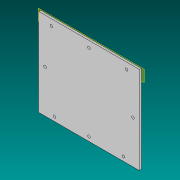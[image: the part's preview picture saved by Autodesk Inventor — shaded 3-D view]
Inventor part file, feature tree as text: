
AUTODESK INVENTOR PART (.ipt)
format: ipt  version: 2019 (Build 230136000, 136)  size: 124,416 bytes
history: native  units: mm
features: reference x16, extrude x5, sketch x5, other x5, plane x1
ambient origin geometry x8: Origin, YZ Plane, XZ Plane, XY Plane, X Axis, Y Axis, Z Axis, Center Point
bodies: Solid1 (feature_tree)
feature tree (32):
  plane  "Work Plane1"
  extrude  "Extrusion1"  Depth=2.0mm
  extrude  "Extrusion2"  Depth=2.5mm
  extrude  "Extrusion3"  Depth=2.5mm
  extrude  "Extrusion4"  Depth=2.0mm TaperAngle=0.0deg
  extrude  "Extrusion5"  Depth=2.0mm TaperAngle=0.0deg
  sketch  "Sketch1"  dims[d0=2.0mm d1=0.0mm d2=2.5mm]
  reference  "Reference1"
  reference  "Reference2"
  reference  "Reference3"
  reference  "Reference4"
  reference  "Reference5"
  reference  "Reference6"
  reference  "Reference7"
  reference  "Reference8"
  reference  "Reference9"
  reference  "Reference10"
  reference  "Reference11"
  reference  "Reference12"
  reference  "Reference13"
  sketch  "Sketch2"  dims[d3=2.5mm d4=2.5mm]
  sketch  "Sketch3"  dims[d5=2.5mm d6=2.5mm]
  sketch  "Sketch4"  dims[d7=2.5mm d8=2.0mm d9=0.0mm]
  sketch  "Sketch5"  dims[d10=2.0mm d11=0.0mm d12=2.0mm d13=0.0mm d21=2.5mm d25=2.5mm d26=2.0mm d27=0.0mm]
  reference  "Reference14"
  reference  "Reference15"
  reference  "Reference16"
  other  "Ensamblaje Reloj LCD 16x2.iam"
  other  "Lateral Derecho:1"
  other  "Lado izquierdo:1"
  other  "Before:1"
  other  "Down:1"
